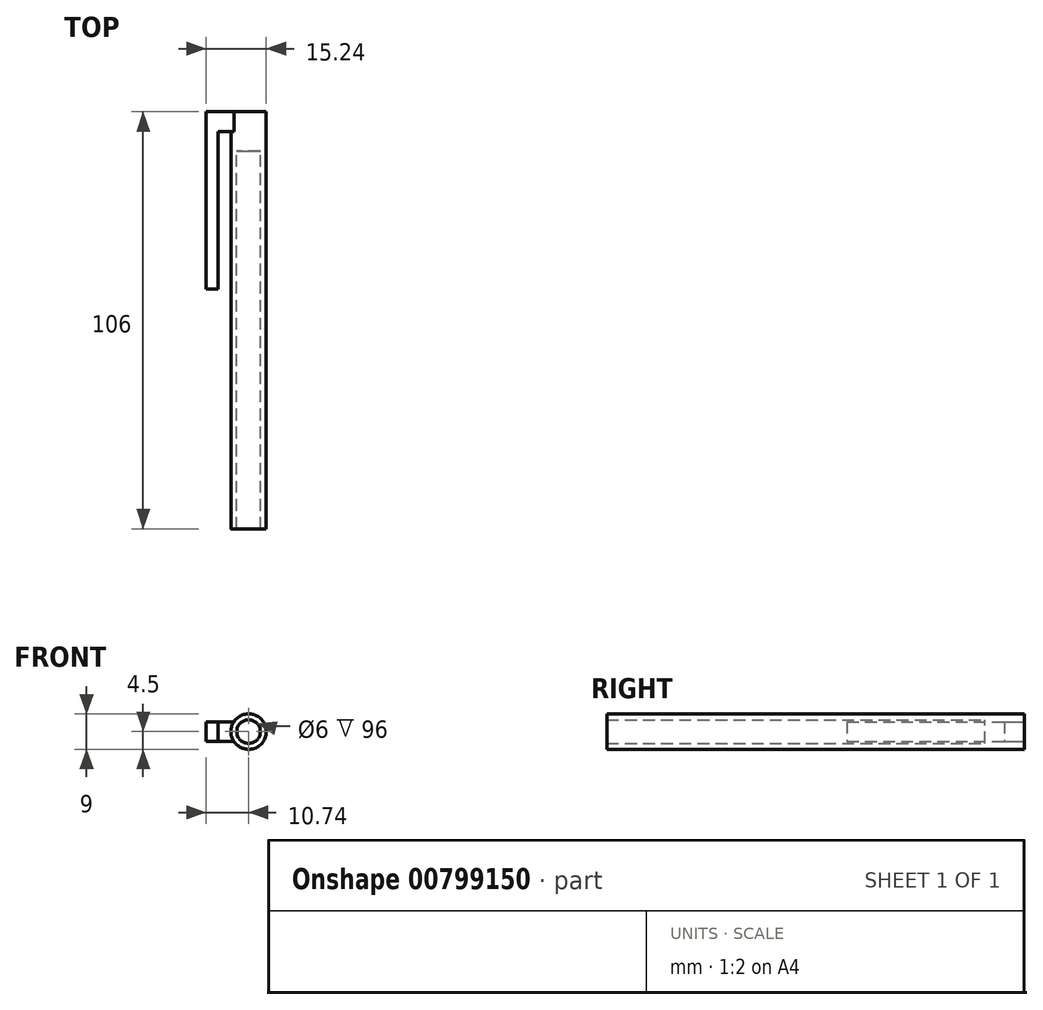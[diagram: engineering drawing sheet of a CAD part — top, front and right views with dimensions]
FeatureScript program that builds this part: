
annotation { "Feature Type Name" : "Feature", "Feature Type Description" : "" }
export const myFeature = defineFeature(function(context is Context, id is Id, definition is map)
    precondition{}
    {
        {
            var Q0;
            Q0=qCreatedBy(makeId("Front.planeOp"),FACE);
            var sketch = newSketch(context, id + "F0", { "sketchPlane" : qUnion([Q0])});
            skCircle(sketch, "E0", {"center": v(0, 0) * mm, "radius": 4.5 * mm});
            skCircle(sketch, "E1", {"center": v(0, 0) * mm, "radius": 3 * mm});
            skLineSegment(sketch, "E2", {"start": v(-3.74, 2.5) * mm, "end": v(-7.74, 2.5) * mm});
            skLineSegment(sketch, "E3", {"start": v(-3.74, -2.5) * mm, "end": v(-7.74, -2.5) * mm});
            skLineSegment(sketch, "E4", {"start": v(-7.74, 2.5) * mm, "end": v(-7.74, -2.5) * mm});
            skLineSegment(sketch, "E5", {"start": v(-7.74, 2.5) * mm, "end": v(-10.74, 2.5) * mm});
            skLineSegment(sketch, "E6", {"start": v(-10.74, 2.5) * mm, "end": v(-10.74, -2.5) * mm});
            skLineSegment(sketch, "E7", {"start": v(-10.74, -2.5) * mm, "end": v(-7.74, -2.5) * mm});
            skSolve(sketch);
        }
        {
            var Q0;
            Q0=makeQuery(id+"F0.imprint","IMPRINT",FACE,{"disambiguationData":[TD([[makeQuery(id+"F0.imprint","IMPRINT",EDGE,{"derivedFrom":sQuery(id+"F0.wireOp",EDGE,"E0")}),1.0]])]});
            extrude(context, id + "F1", {"entities" : qUnion([Q0]), "depth" : 106 * mm, "offsetDistance" : 25.4 * mm});
        }
        {
            var Q0;
            Q0=makeQuery(id+"F0.imprint","IMPRINT",FACE,{"disambiguationData":[TD([[makeQuery(id+"F0.imprint","IMPRINT",EDGE,{"derivedFrom":sQuery(id+"F0.wireOp",EDGE,"E1")}),1.0]])]});
            extrude(context, id + "F2", {"entities" : qUnion([Q0]), "operationType" : NewBodyOperationType.ADD, "depth" : 10 * mm, "offsetDistance" : 25.4 * mm});
        }
        {
            var Q0;
            {var subQ0=sQuery(id+"F0.wireOp",EDGE,"E2");Q0=makeQuery(id+"F0.imprint","IMPRINT",FACE,{"disambiguationData":[TD([[makeQuery(id+"F0.imprint","IMPRINT",EDGE,{"derivedFrom":subQ0}),1.0]])]});}
            extrude(context, id + "F3", {"entities" : qUnion([Q0]), "operationType" : NewBodyOperationType.ADD, "depth" : 5 * mm, "offsetDistance" : 25.4 * mm});
        }
        {
            var Q0;
            Q0=makeQuery(id+"F0.imprint","IMPRINT",FACE,{"disambiguationData":[TD([[makeQuery(id+"F0.imprint","IMPRINT",EDGE,{"derivedFrom":sQuery(id+"F0.wireOp",EDGE,"E4")}),-1.0]])]});
            extrude(context, id + "F4", {"entities" : qUnion([Q0]), "operationType" : NewBodyOperationType.ADD, "depth" : 45 * mm, "offsetDistance" : 25.4 * mm});
        }
    });
